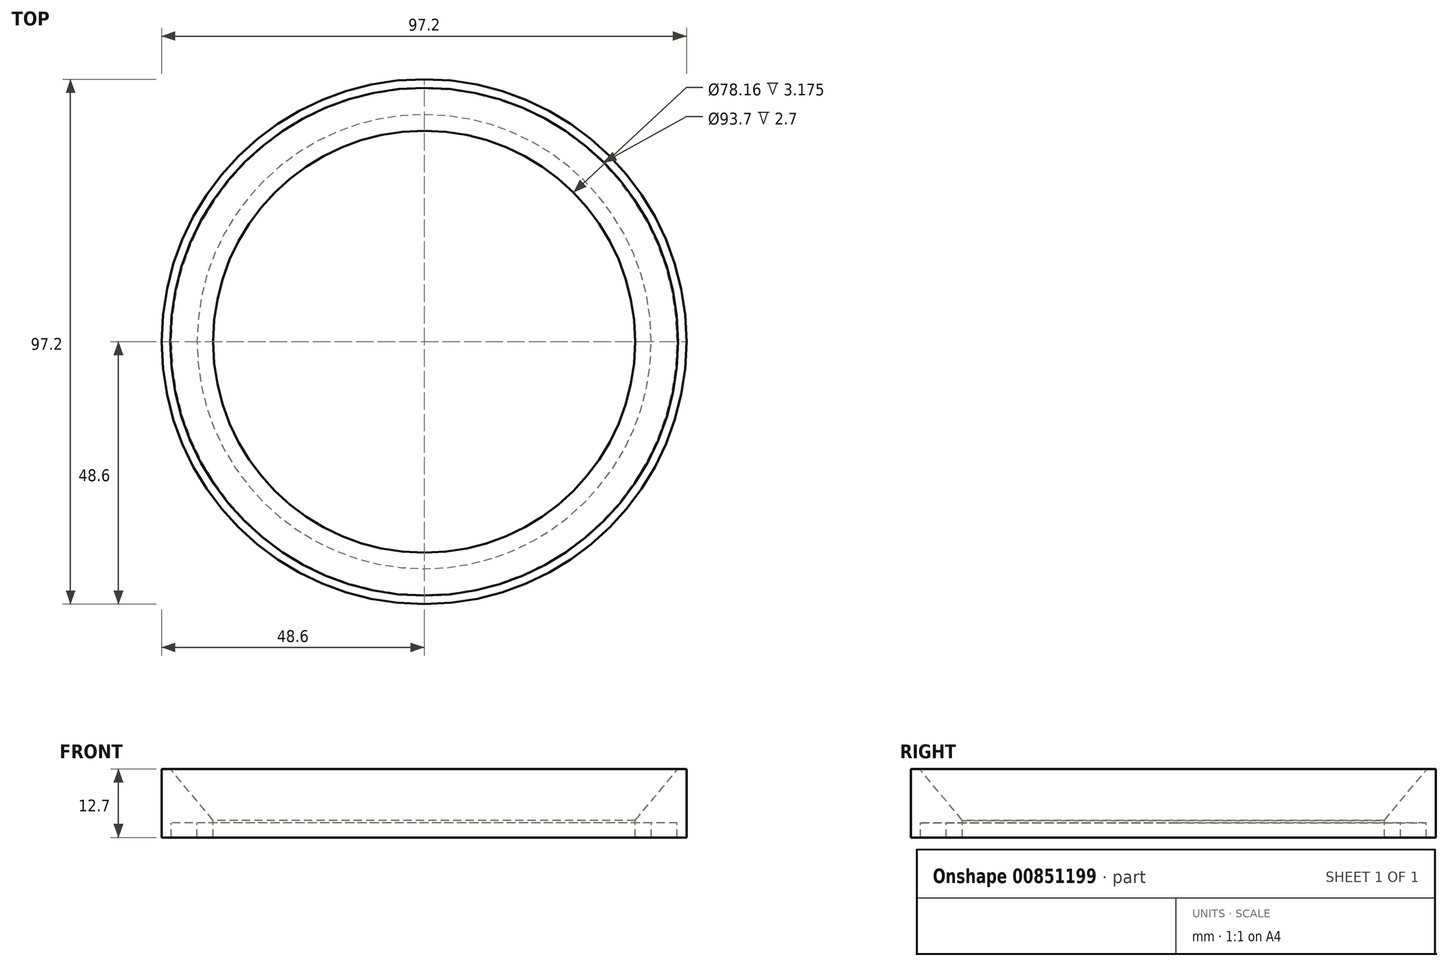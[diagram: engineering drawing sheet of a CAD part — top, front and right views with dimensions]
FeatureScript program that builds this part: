
annotation { "Feature Type Name" : "Feature", "Feature Type Description" : "" }
export const myFeature = defineFeature(function(context is Context, id is Id, definition is map)
    precondition{}
    {
        {
            var Q0;
            Q0=qCreatedBy(makeId("Front.planeOp"),FACE);
            var sketch = newSketch(context, id + "F0", { "sketchPlane" : qUnion([Q0])});
            skLineSegment(sketch, "E0", {"start": v(48.6, 0) * mm, "end": v(48.6, 12.7) * mm});
            skLineSegment(sketch, "E1", {"start": v(48.6, 12.7) * mm, "end": v(47.02, 12.7) * mm});
            skLineSegment(sketch, "E2", {"start": v(47.02, 12.7) * mm, "end": v(39.08, 3.17) * mm});
            skLineSegment(sketch, "E3", {"start": v(39.08, 3.17) * mm, "end": v(39.08, 0) * mm});
            skArc(sketch, "E4", {"start": v(45.95, 0) * mm, "mid": v(44.45, 1.06) * mm, "end": v(42.95, 0) * mm, "construction": true});
            skLineSegment(sketch, "E5", {"start": v(39.08, 0) * mm, "end": v(42.95, 0) * mm});
            skLineSegment(sketch, "E6", {"start": v(48.6, 0) * mm, "end": v(45.95, 0) * mm});
            skLineSegment(sketch, "E7", {"start": v(41.21, 1.06) * mm, "end": v(46.42, 1.06) * mm, "construction": true});
            skLineSegment(sketch, "E8", {"start": v(0, 19.6) * mm, "end": v(0, -27.09) * mm, "construction": true});
            skLineSegment(sketch, "E9.bottom", {"start": v(42.05, 0) * mm, "end": v(42.95, 0) * mm});
            skLineSegment(sketch, "E9.top", {"start": v(42.05, 2.7) * mm, "end": v(46.85, 2.7) * mm});
            skLineSegment(sketch, "E9.left", {"start": v(42.05, 0) * mm, "end": v(42.05, 2.7) * mm});
            skLineSegment(sketch, "E9.right", {"start": v(46.85, 0) * mm, "end": v(46.85, 2.7) * mm});
            skLineSegment(sketch, "E10.trimOffspring", {"start": v(45.95, 0) * mm, "end": v(46.85, 0) * mm});
            skSolve(sketch);
        }
        {
            var Q0;
            Q0=makeQuery(id+"F0.imprint","IMPRINT",FACE,{"disambiguationData":[TD([[makeQuery(id+"F0.imprint","IMPRINT",EDGE,{"derivedFrom":sQuery(id+"F0.wireOp",EDGE,"E0")}),1.0]])]});
            var Q1;
            Q1=sQuery(id+"F0.wireOp",EDGE,"E8");
            revolve(context, id + "F1", {"surfaceOperationType" : NewSurfaceOperationType.NEW, "entities" : qUnion([Q0]), "axis" : qUnion([Q1]), "revolveType" : RevolveType.FULL});
        }
    });
